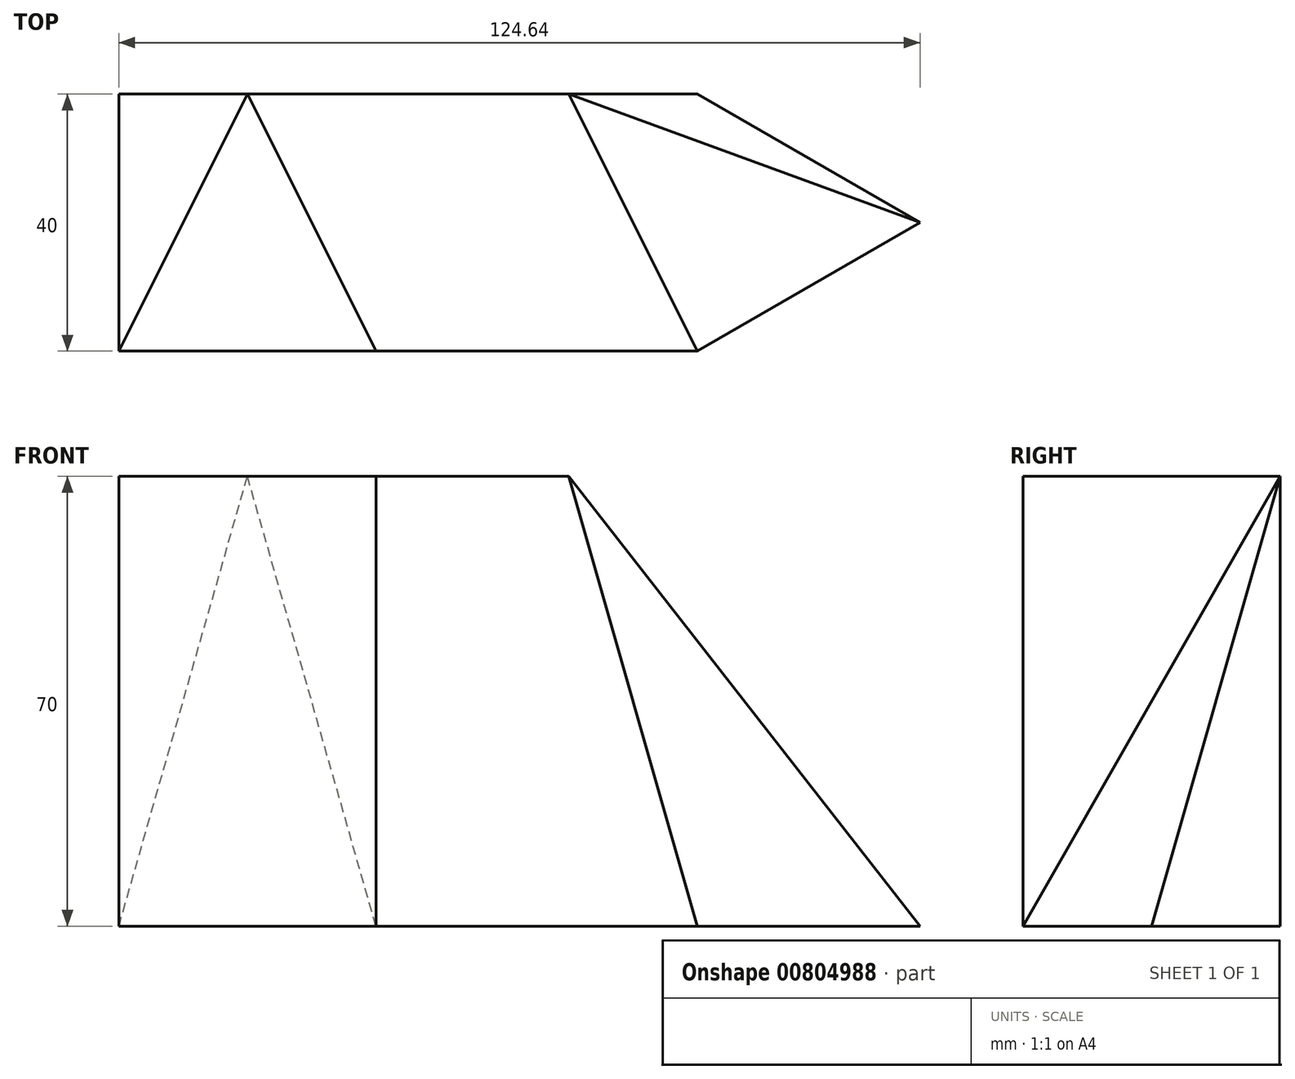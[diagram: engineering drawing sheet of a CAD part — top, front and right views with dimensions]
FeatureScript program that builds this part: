
annotation { "Feature Type Name" : "Feature", "Feature Type Description" : "" }
export const myFeature = defineFeature(function(context is Context, id is Id, definition is map)
    precondition{}
    {
        {
            var Q0;
            Q0=qCreatedBy(makeId("Top.planeOp"),FACE);
            var sketch = newSketch(context, id + "F0", { "sketchPlane" : qUnion([Q0])});
            skLineSegment(sketch, "E0.bottom", {"start": v(-20, 20) * mm, "end": v(20, 20) * mm});
            skLineSegment(sketch, "E0.top", {"start": v(-20, -20) * mm, "end": v(20, -20) * mm});
            skLineSegment(sketch, "E0.left", {"start": v(-20, 20) * mm, "end": v(-20, -20) * mm});
            skLineSegment(sketch, "E0.right", {"start": v(20, 20) * mm, "end": v(20, -20) * mm});
            skPoint(sketch, "E0.middle", {"position": v(0, 0) * mm});
            skLineSegment(sketch, "E1.bottom", {"start": v(20, 20) * mm, "end": v(70, 20) * mm});
            skLineSegment(sketch, "E1.top", {"start": v(20, -20) * mm, "end": v(70, -20) * mm});
            skLineSegment(sketch, "E1.right", {"start": v(70, 20) * mm, "end": v(70, -20) * mm});
            skLineSegment(sketch, "E2", {"start": v(70, 20) * mm, "end": v(104.64, 0) * mm});
            skLineSegment(sketch, "E3", {"start": v(104.64, 0) * mm, "end": v(70, -20) * mm});
            skSolve(sketch);
        }
        {
            var Q0;
            Q0=qCreatedBy(makeId("Top.planeOp"),FACE);
            cPlane(context, id + "F1", {"entities" : qUnion([Q0]), "cplaneType" : CPlaneType.OFFSET, "offset" : 70 * mm, "width" : 150 * mm, "height" : 150 * mm});
        }
        {
            var Q0;
            Q0=qCreatedBy(id+"F1.planeOp",FACE);
            var sketch = newSketch(context, id + "F2", { "sketchPlane" : qUnion([Q0])});
            skPoint(sketch, "E4.0", {"position": v(0, 20) * mm});
            skPoint(sketch, "E5.0", {"position": v(-20, -20) * mm});
            skPoint(sketch, "E6.0", {"position": v(20, -20) * mm});
            skLineSegment(sketch, "E7", {"start": v(-20, -20) * mm, "end": v(20, -20) * mm});
            skLineSegment(sketch, "E8", {"start": v(0, 20) * mm, "end": v(20, -20) * mm});
            skLineSegment(sketch, "E9", {"start": v(-20, -20) * mm, "end": v(0, 20) * mm});
            skSolve(sketch);
        }
        {
            var Q0;
            Q0=makeQuery(id+"F0.imprint","IMPRINT",FACE,{"disambiguationData":[TD([[makeQuery(id+"F0.imprint","IMPRINT",EDGE,{"derivedFrom":sQuery(id+"F0.wireOp",EDGE,"E0.bottom")}),-1.0]])]});
            var Q1;
            Q1=sQuery(id+"F2.wireOp",VERTEX,"E4.0");
            loft(context, id + "F3", {"sheetProfilesArray" : [{ "sheetProfileEntities" : qUnion([Q0]) }, { "sheetProfileEntities" : qUnion([Q1]) }]});
        }
        {
            var Q0;
            Q0=qCreatedBy(makeId("Front.planeOp"),FACE);
            cPlane(context, id + "F4", {"entities" : qUnion([Q0]), "cplaneType" : CPlaneType.OFFSET, "offset" : 20 * mm, "width" : 150 * mm, "height" : 150 * mm});
        }
        {
            var Q0;
            Q0=qCreatedBy(id+"F4.planeOp",FACE);
            var sketch = newSketch(context, id + "F5", { "sketchPlane" : qUnion([Q0])});
            skPoint(sketch, "E10.0", {"position": v(-20, 0) * mm});
            skPoint(sketch, "E11.0", {"position": v(20, 0) * mm});
            skPoint(sketch, "E12.0", {"position": v(20, 70) * mm});
            skPoint(sketch, "E13.0", {"position": v(-20, 70) * mm});
            skLineSegment(sketch, "E14.bottom", {"start": v(-20, 70) * mm, "end": v(20, 70) * mm});
            skLineSegment(sketch, "E14.top", {"start": v(-20, 0) * mm, "end": v(20, 0) * mm});
            skLineSegment(sketch, "E14.left", {"start": v(-20, 70) * mm, "end": v(-20, 0) * mm});
            skLineSegment(sketch, "E14.right", {"start": v(20, 70) * mm, "end": v(20, 0) * mm});
            skLineSegment(sketch, "E15", {"start": v(50, 70) * mm, "end": v(70, 0) * mm});
            skSolve(sketch);
        }
        {
            var Q1;
            Q1=makeQuery(id+"F5.imprint","IMPRINT",FACE,{"disambiguationData":[TD([[makeQuery(id+"F5.imprint","IMPRINT",EDGE,{"derivedFrom":sQuery(id+"F5.wireOp",EDGE,"E14.bottom")}),-1.0]])]});
            var Q2;
            Q2=sQuery(id+"F2.wireOp",VERTEX,"E4.0");
            loft(context, id + "F6", {"operationType" : NewBodyOperationType.ADD, "sheetProfilesArray" : [{ "sheetProfileEntities" : qUnion([Q1]) }, { "sheetProfileEntities" : qUnion([Q2]) }]});
        }
        {
            var Q0;
            Q0=qCreatedBy(makeId("Right.planeOp"),FACE);
            var Q1;
            Q1=sQuery(id+"F5.wireOp",EDGE,"E15");
            cPlane(context, id + "F7", {"entities" : qUnion([Q0, Q1]), "cplaneType" : CPlaneType.LINE_ANGLE, "offset" : 25 * mm, "angle" : 0 * degree, "width" : 150 * mm, "height" : 150 * mm});
        }
        {
            var Q0;
            Q0=qCreatedBy(id+"F7.planeOp",FACE);
            var sketch = newSketch(context, id + "F8", { "sketchPlane" : qUnion([Q0])});
            skLineSegment(sketch, "E16.0", {"start": v(20, 53.57) * mm, "end": v(20, -19.23) * mm});
            skLineSegment(sketch, "E17", {"start": v(20, -19.23) * mm, "end": v(-20, -19.23) * mm});
            skLineSegment(sketch, "E18", {"start": v(-20, -19.23) * mm, "end": v(-20, 53.57) * mm});
            skLineSegment(sketch, "E19", {"start": v(20, -19.23) * mm, "end": v(-20, 53.57) * mm});
            skSolve(sketch);
        }
        {
            var Q1;
            Q1=makeQuery(id+"F8.imprint","IMPRINT",FACE,{"disambiguationData":[TD([[makeQuery(id+"F8.imprint","IMPRINT",EDGE,{"derivedFrom":sQuery(id+"F8.wireOp",EDGE,"E17")}),-1.0]])]});
            var Q2;
            Q2=makeQuery(id+"F3.opLoft","SWEPT_FACE",FACE,{"disambiguationData":[OSD([sQuery(id+"F0.wireOp",EDGE,"E0.bottom"),sQuery(id+"F0.wireOp",EDGE,"E0.top"),sQuery(id+"F0.wireOp",EDGE,"E1.bottom"),sQuery(id+"F0.wireOp",EDGE,"E1.top"),sQuery(id+"F0.wireOp",EDGE,"E0.right")])]});
            loft(context, id + "F9", {"operationType" : NewBodyOperationType.ADD, "sheetProfilesArray" : [{ "sheetProfileEntities" : qUnion([Q1]) }, { "sheetProfileEntities" : qUnion([Q2]) }]});
        }
        {
            var Q1;
            Q1=makeQuery(id+"F0.imprint","IMPRINT",FACE,{"disambiguationData":[TD([[makeQuery(id+"F0.imprint","IMPRINT",EDGE,{"derivedFrom":sQuery(id+"F0.wireOp",EDGE,"E1.right")}),1.0]])]});
            var Q2;
            Q2=makeQuery(id+"F9.opLoft","MID_CAP_VERTEX",VERTEX,{"disambiguationData":[OSD([sQuery(id+"F8.wireOp",EDGE,"E18"),sQuery(id+"F8.wireOp",EDGE,"E19")])],"capPos":0.0});
            loft(context, id + "F10", {"operationType" : NewBodyOperationType.ADD, "sheetProfilesArray" : [{ "sheetProfileEntities" : qUnion([Q1]) }, { "sheetProfileEntities" : qUnion([Q2]) }]});
        }
    });
